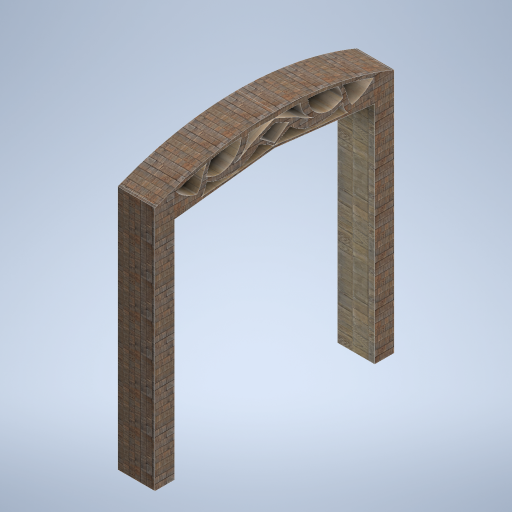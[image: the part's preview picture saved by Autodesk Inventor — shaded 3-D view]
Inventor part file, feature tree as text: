
AUTODESK INVENTOR PART (.ipt)
format: ipt  version: 2024.2 (Build 282272000, 272)  size: 473,088 bytes
history: native  units: mm
features: extrude x1, sketch x1
ambient origin geometry x8: Origin, YZ Plane, XZ Plane, XY Plane, X Axis, Y Axis, Z Axis, Center Point
bodies: Solid1 (feature_tree)
feature tree (2):
  extrude  "Extrusion1"  Depth=380.0mm
  sketch  "Sketch1"  dims[d0=200.0mm d1=2300.0mm d5=380.0mm d6=0.0mm]
